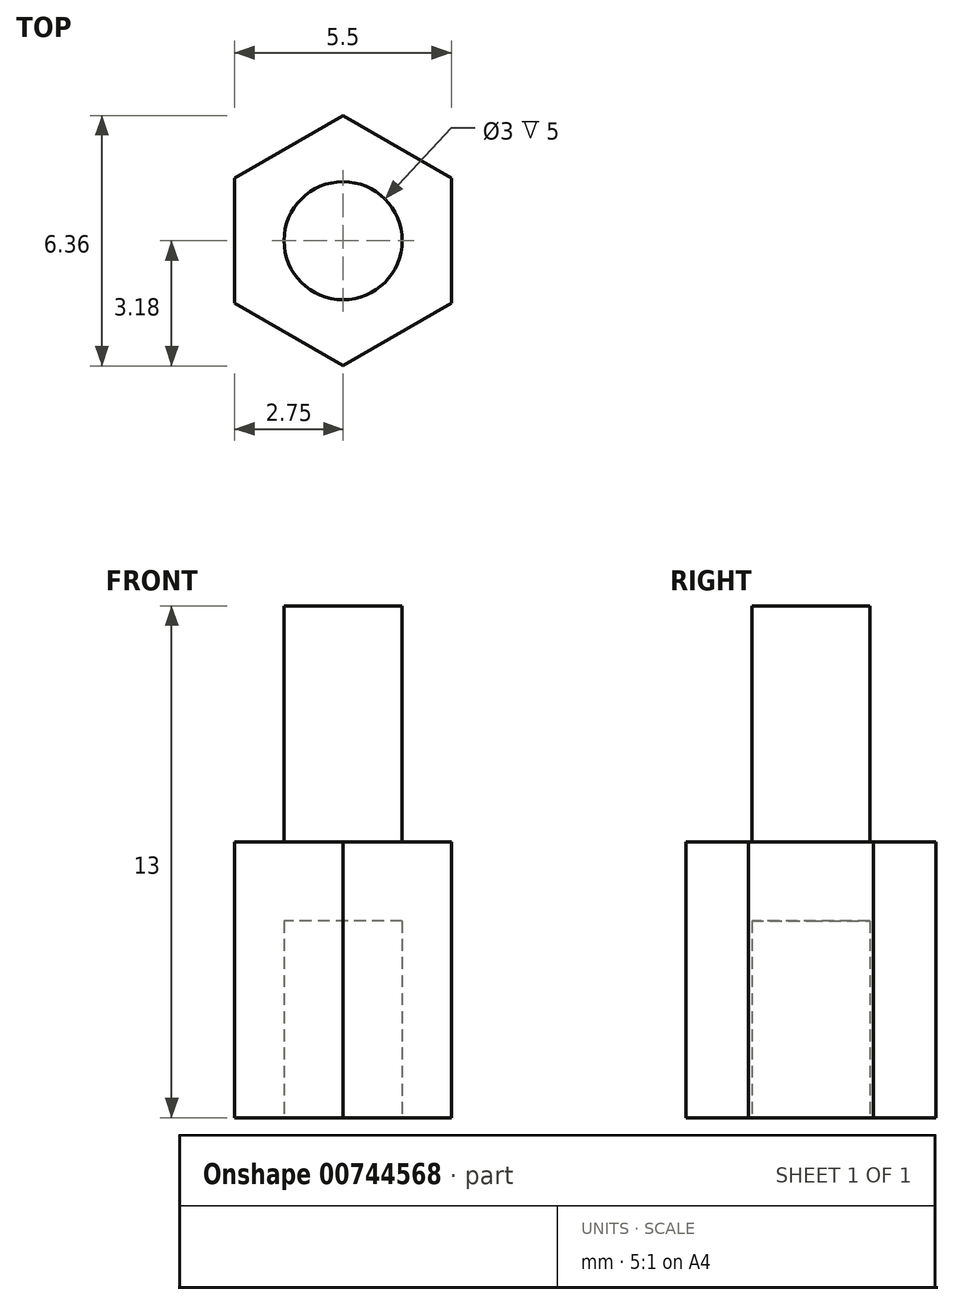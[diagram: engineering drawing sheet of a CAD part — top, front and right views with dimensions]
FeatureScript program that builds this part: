
annotation { "Feature Type Name" : "Feature", "Feature Type Description" : "" }
export const myFeature = defineFeature(function(context is Context, id is Id, definition is map)
    precondition{}
    {
        {
            var Q0;
            Q0=qCreatedBy(makeId("Top.planeOp"),FACE);
            var sketch = newSketch(context, id + "F0", { "sketchPlane" : qUnion([Q0])});
            skCircle(sketch, "E0.cCircle", {"center": v(0, 0) * mm, "radius": 3.18 * mm, "construction": true});
            skLineSegment(sketch, "E0.0", {"start": v(2.75, 1.59) * mm, "end": v(2.75, -1.59) * mm});
            skLineSegment(sketch, "E0.1", {"start": v(2.75, -1.59) * mm, "end": v(0, -3.18) * mm});
            skLineSegment(sketch, "E0.2", {"start": v(0, -3.18) * mm, "end": v(-2.75, -1.59) * mm});
            skLineSegment(sketch, "E0.3", {"start": v(-2.75, -1.59) * mm, "end": v(-2.75, 1.59) * mm});
            skLineSegment(sketch, "E0.4", {"start": v(-2.75, 1.59) * mm, "end": v(0, 3.18) * mm});
            skLineSegment(sketch, "E0.5", {"start": v(0, 3.18) * mm, "end": v(2.75, 1.59) * mm});
            skCircle(sketch, "E1", {"center": v(0, 0) * mm, "radius": 1.5 * mm});
            skSolve(sketch);
        }
        {
            var Q0;
            Q0=qSketchRegion(id+"F0",true);
            extrude(context, id + "F1", {"entities" : qUnion([Q0]), "depth" : 7 * mm, "offsetDistance" : 25 * mm});
        }
        {
            var Q0;
            Q0=makeQuery(id+"F1.opExtrude","CAP_FACE",FACE,{"disambiguationData":[OSD([sQuery(id+"F0.wireOp",EDGE,"E0.0"),sQuery(id+"F0.wireOp",EDGE,"E0.1"),sQuery(id+"F0.wireOp",EDGE,"E0.2"),sQuery(id+"F0.wireOp",EDGE,"E0.3"),sQuery(id+"F0.wireOp",EDGE,"E0.4"),sQuery(id+"F0.wireOp",EDGE,"E0.5")])],"isStart":false});
            var sketch = newSketch(context, id + "F2", { "sketchPlane" : qUnion([Q0])});
            skCircle(sketch, "E2", {"center": v(0, 0) * mm, "radius": 1.5 * mm});
            skSolve(sketch);
        }
        {
            var Q0;
            Q0=qSketchRegion(id+"F2",true);
            extrude(context, id + "F3", {"entities" : qUnion([Q0]), "operationType" : NewBodyOperationType.ADD, "depth" : 6 * mm, "offsetDistance" : 25 * mm, "hasSecondDirection" : true, "secondDirectionOppositeDirection" : true, "secondDirectionDepth" : 2 * mm, "hasSecondDirectionDraft" : true, "secondDirectionDraftAngle" : 3 * degree});
        }
        {
            var Q0;
            Q0=makeQuery(id+"F0.imprint","IMPRINT",FACE,{"disambiguationData":[TD([[makeQuery(id+"F0.imprint","IMPRINT",EDGE,{"derivedFrom":sQuery(id+"F0.wireOp",EDGE,"E1")}),1.0]])]});
            extrude(context, id + "F4", {"entities" : qUnion([Q0]), "operationType" : NewBodyOperationType.REMOVE, "depth" : 5 * mm, "offsetDistance" : 25 * mm});
        }
    });
